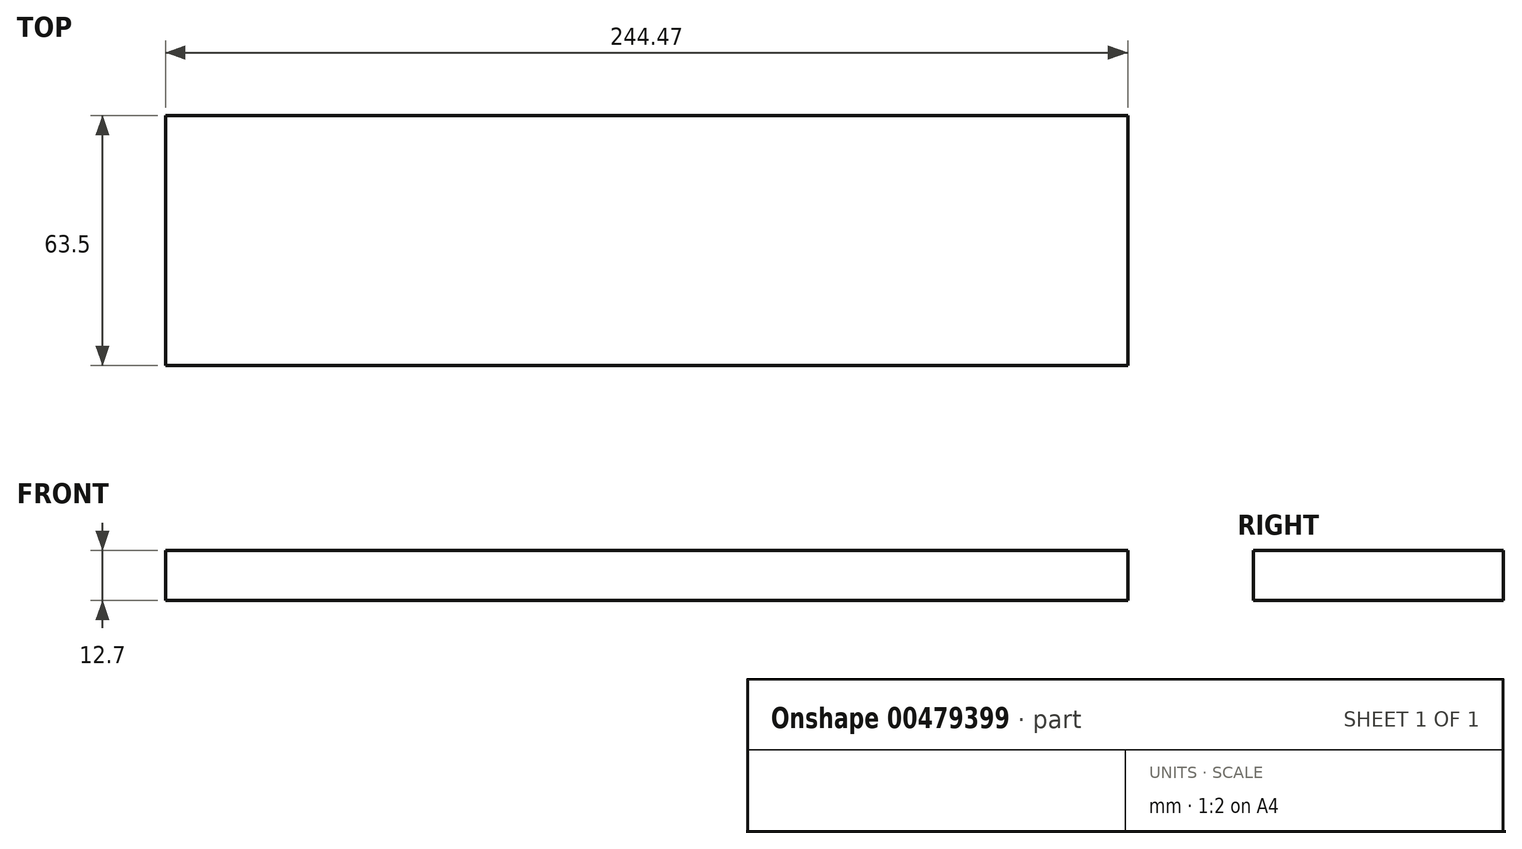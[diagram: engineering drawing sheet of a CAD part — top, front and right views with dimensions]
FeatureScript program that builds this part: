
annotation { "Feature Type Name" : "Feature", "Feature Type Description" : "" }
export const myFeature = defineFeature(function(context is Context, id is Id, definition is map)
    precondition{}
    {
        {
            var Q0;
            Q0=qCreatedBy(makeId("Top.planeOp"),FACE);
            var sketch = newSketch(context, id + "F0", { "sketchPlane" : qUnion([Q0])});
            skLineSegment(sketch, "E0.bottom", {"start": v(0, 0) * mm, "end": v(244.47, 0) * mm});
            skLineSegment(sketch, "E0.top", {"start": v(0, 63.5) * mm, "end": v(244.48, 63.5) * mm});
            skLineSegment(sketch, "E0.left", {"start": v(0, 0) * mm, "end": v(0, 63.5) * mm});
            skLineSegment(sketch, "E0.right", {"start": v(244.48, 0) * mm, "end": v(244.48, 63.5) * mm});
            skSolve(sketch);
        }
        {
            var Q0;
            Q0=makeQuery(id+"F0.imprint","IMPRINT",FACE,{"disambiguationData":[TD([[makeQuery(id+"F0.imprint","IMPRINT",EDGE,{"derivedFrom":sQuery(id+"F0.wireOp",EDGE,"E0.bottom")}),1.0]])]});
            extrude(context, id + "F1", {"entities" : qUnion([Q0]), "depth" : 12.7 * mm});
        }
    });
